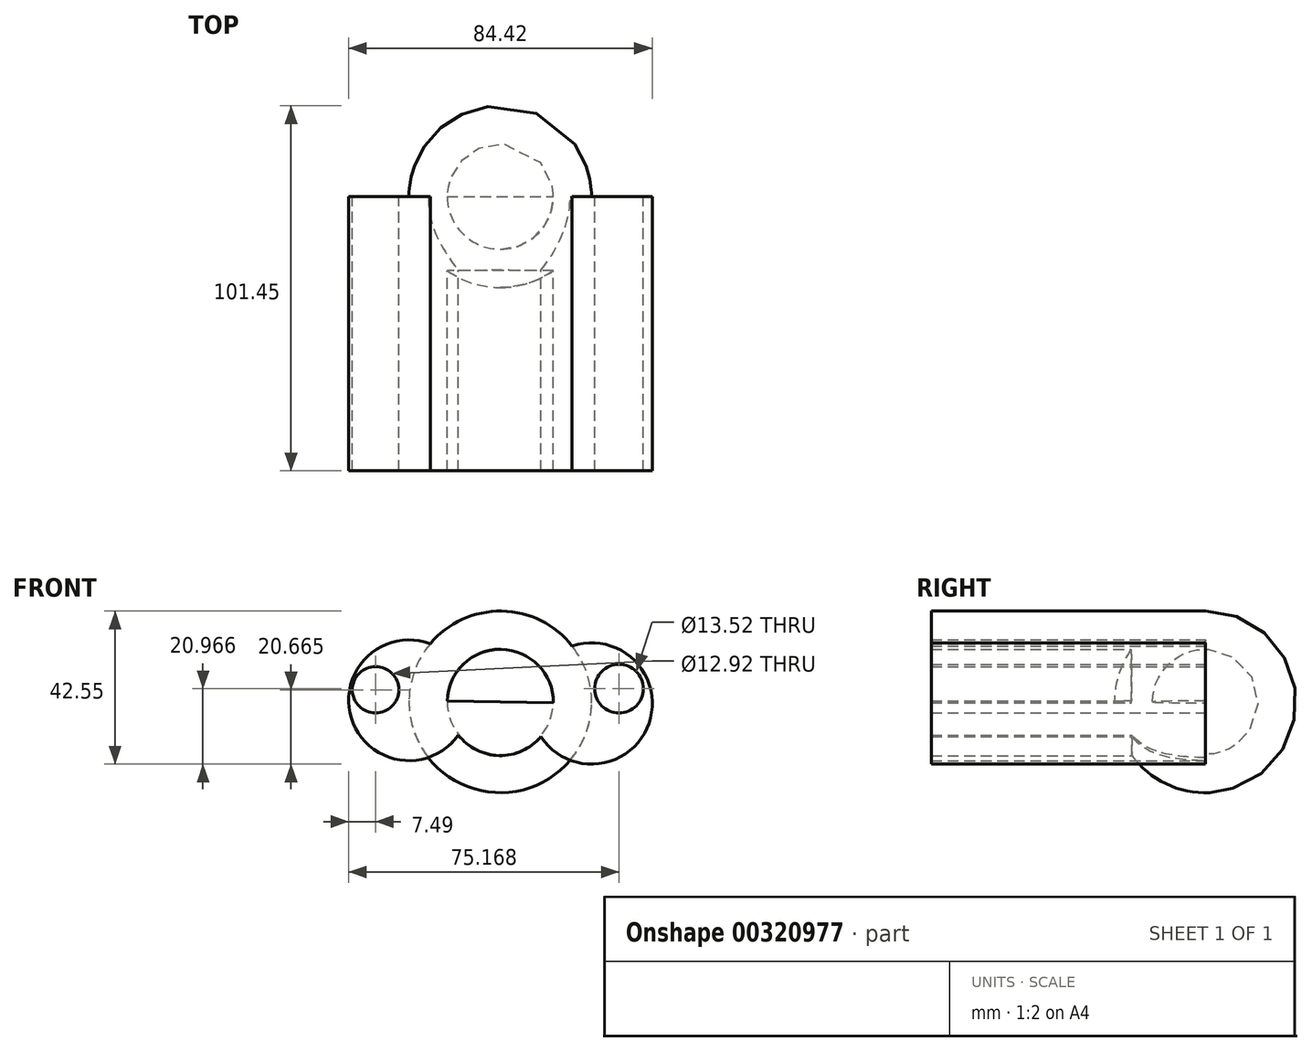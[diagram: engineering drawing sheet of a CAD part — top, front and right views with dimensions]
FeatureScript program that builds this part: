
annotation { "Feature Type Name" : "Feature", "Feature Type Description" : "" }
export const myFeature = defineFeature(function(context is Context, id is Id, definition is map)
    precondition{}
    {
        {
            var Q0;
            Q0=qCreatedBy(makeId("Front.planeOp"),FACE);
            var sketch = newSketch(context, id + "F0", { "sketchPlane" : qUnion([Q0])});
            skArc(sketch, "E0", {"start": v(35.77, 21.16) * mm, "mid": v(10.82, 46.85) * mm, "end": v(-15.02, 22.04) * mm});
            skLineSegment(sketch, "E1", {"start": v(-15.02, 22.04) * mm, "end": v(35.77, 21.16) * mm});
            skCircle(sketch, "E2", {"center": v(35.77, 21.16) * mm, "radius": 16.86 * mm});
            skCircle(sketch, "E3", {"center": v(-15.02, 22.04) * mm, "radius": 16.78 * mm});
            skCircle(sketch, "E4", {"center": v(10.38, 21.45) * mm, "radius": 14.78 * mm});
            skSolve(sketch);
        }
        {
            var Q0;
            Q0=makeQuery(id+"F0.imprint","IMPRINT",FACE,{"disambiguationData":[TD([[makeQuery(id+"F0.imprint","IMPRINT",EDGE,{"derivedFrom":sQuery(id+"F0.wireOp",EDGE,"E0")}),1.0]])]});
            var Q1;
            Q1=sQuery(id+"F0.wireOp",EDGE,"E1");
            revolve(context, id + "F1", {"entities" : qUnion([Q0]), "axis" : qUnion([Q1]), "revolveType" : RevolveType.FULL});
        }
        {
            var Q0;
            Q0 = qSketchRegion(id + "F0", true);
            extrude(context, id + "F2", {"entities" : qUnion([Q0]), "operationType" : NewBodyOperationType.ADD, "depth" : 76.2 * mm});
        }
        {
            var Q0;
            Q0=qCreatedBy(makeId("Front.planeOp"),FACE);
            var sketch = newSketch(context, id + "F3", { "sketchPlane" : qUnion([Q0])});
            skCircle(sketch, "E5", {"center": v(-24.3, 24.97) * mm, "radius": 6.46 * mm});
            skCircle(sketch, "E6", {"center": v(43.38, 25.27) * mm, "radius": 6.76 * mm});
            skSolve(sketch);
        }
        {
            var Q0;
            Q0=makeQuery(id+"F3.imprint","IMPRINT",FACE,{"disambiguationData":[TD([[makeQuery(id+"F3.imprint","IMPRINT",EDGE,{"derivedFrom":sQuery(id+"F3.wireOp",EDGE,"E6")}),1.0]])]});
            var Q1;
            Q1=makeQuery(id+"F3.imprint","IMPRINT",FACE,{"disambiguationData":[TD([[makeQuery(id+"F3.imprint","IMPRINT",EDGE,{"derivedFrom":sQuery(id+"F3.wireOp",EDGE,"E5")}),1.0]])]});
            extrude(context, id + "F4", {"entities" : qUnion([Q0, Q1]), "operationType" : NewBodyOperationType.REMOVE, "endBound" : BoundingType.THROUGH_ALL, "depth" : 50.8 * mm});
        }
    });
